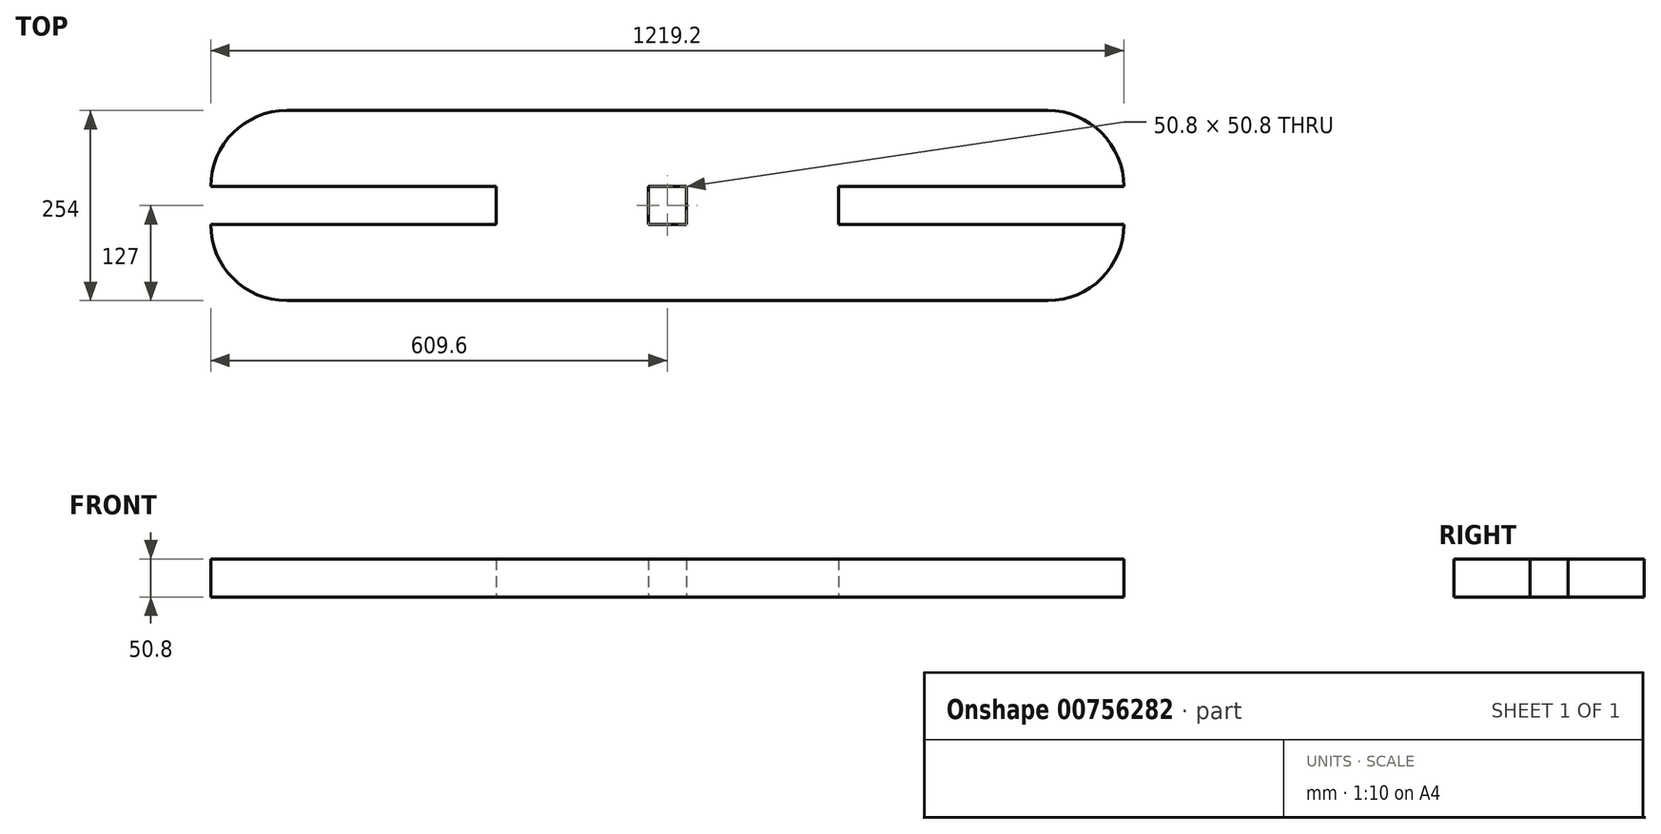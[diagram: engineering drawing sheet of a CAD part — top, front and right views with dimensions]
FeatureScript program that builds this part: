
annotation { "Feature Type Name" : "Feature", "Feature Type Description" : "" }
export const myFeature = defineFeature(function(context is Context, id is Id, definition is map)
    precondition{}
    {
        {
            var Q0;
            Q0=qCreatedBy(makeId("Top.planeOp"),FACE);
            var sketch = newSketch(context, id + "F0", { "sketchPlane" : qUnion([Q0])});
            skLineSegment(sketch, "E0.bottom", {"start": v(508, 127) * mm, "end": v(-508, 127) * mm});
            skLineSegment(sketch, "E0.top", {"start": v(508, -127) * mm, "end": v(-508, -127) * mm});
            skPoint(sketch, "E0.middle", {"position": v(0, 0) * mm});
            skLineSegment(sketch, "E1.bottom", {"start": v(-228.6, 25.4) * mm, "end": v(-609.6, 25.4) * mm});
            skLineSegment(sketch, "E1.top", {"start": v(-228.6, -25.4) * mm, "end": v(-609.6, -25.4) * mm});
            skLineSegment(sketch, "E1.left", {"start": v(-228.6, 25.4) * mm, "end": v(-228.6, -25.4) * mm});
            skPoint(sketch, "E1.middle", {"position": v(-419.1, 0) * mm});
            skLineSegment(sketch, "E2.bottom", {"start": v(228.6, 25.4) * mm, "end": v(609.6, 25.4) * mm});
            skLineSegment(sketch, "E2.top", {"start": v(228.6, -25.4) * mm, "end": v(609.6, -25.4) * mm});
            skLineSegment(sketch, "E2.left", {"start": v(228.6, 25.4) * mm, "end": v(228.6, -25.4) * mm});
            skPoint(sketch, "E2.middle", {"position": v(419.1, 0) * mm});
            skLineSegment(sketch, "E3", {"start": v(-609.6, 25.4) * mm, "end": v(-609.6, 25.4) * mm});
            skLineSegment(sketch, "E4", {"start": v(-609.6, -25.4) * mm, "end": v(-609.6, -25.4) * mm});
            skLineSegment(sketch, "E5", {"start": v(609.6, -25.4) * mm, "end": v(609.6, -25.4) * mm});
            skLineSegment(sketch, "E6", {"start": v(609.6, 25.4) * mm, "end": v(609.6, 25.4) * mm});
            skPoint(sketch, "E7.visualSharp", {"position": v(-609.6, 127) * mm});
            skArc(sketch, "E7.filletArc", {"start": v(-508, 127) * mm, "mid": v(-579.84, 97.24) * mm, "end": v(-609.6, 25.4) * mm});
            skPoint(sketch, "E8.visualSharp", {"position": v(-609.6, -127) * mm});
            skArc(sketch, "E8.filletArc", {"start": v(-609.6, -25.4) * mm, "mid": v(-579.84, -97.24) * mm, "end": v(-508, -127) * mm});
            skPoint(sketch, "E9.visualSharp", {"position": v(609.6, -127) * mm});
            skArc(sketch, "E9.filletArc", {"start": v(508, -127) * mm, "mid": v(579.84, -97.24) * mm, "end": v(609.6, -25.4) * mm});
            skPoint(sketch, "E10.visualSharp", {"position": v(609.6, 127) * mm});
            skArc(sketch, "E10.filletArc", {"start": v(609.6, 25.4) * mm, "mid": v(579.84, 97.24) * mm, "end": v(508, 127) * mm});
            skLineSegment(sketch, "E11.bottom", {"start": v(25.4, 25.4) * mm, "end": v(-25.4, 25.4) * mm});
            skLineSegment(sketch, "E11.top", {"start": v(25.4, -25.4) * mm, "end": v(-25.4, -25.4) * mm});
            skLineSegment(sketch, "E11.left", {"start": v(25.4, 25.4) * mm, "end": v(25.4, -25.4) * mm});
            skLineSegment(sketch, "E11.right", {"start": v(-25.4, 25.4) * mm, "end": v(-25.4, -25.4) * mm});
            skSolve(sketch);
        }
        {
            var Q0;
            Q0=makeQuery(id+"F0.imprint","IMPRINT",FACE,{"disambiguationData":[TD([[makeQuery(id+"F0.imprint","IMPRINT",EDGE,{"derivedFrom":sQuery(id+"F0.wireOp",EDGE,"E0.bottom")}),1.0]])]});
            extrude(context, id + "F1", {"entities" : qUnion([Q0]), "depth" : 50.8 * mm, "offsetDistance" : 25.4 * mm});
        }
    });
